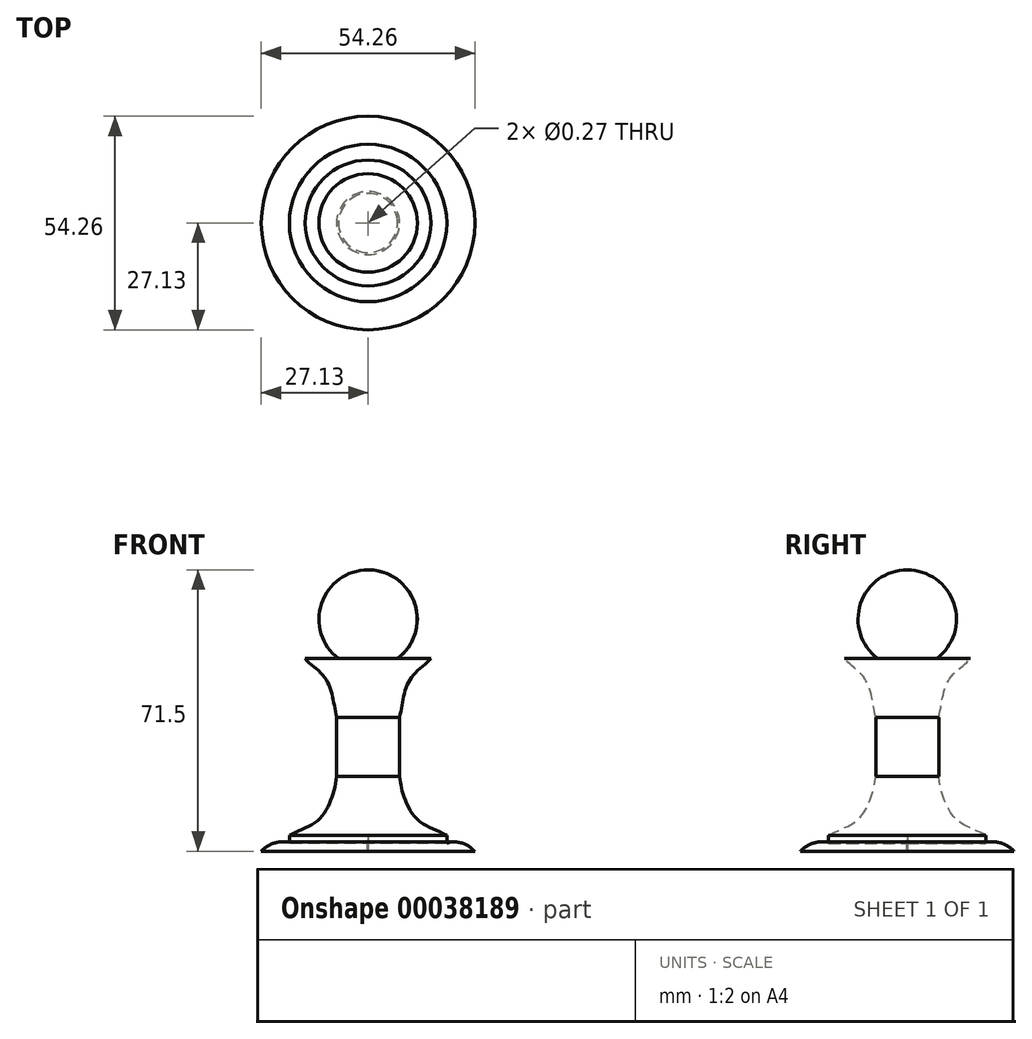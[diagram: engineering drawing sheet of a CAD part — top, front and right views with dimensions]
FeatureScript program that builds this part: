
annotation { "Feature Type Name" : "Feature", "Feature Type Description" : "" }
export const myFeature = defineFeature(function(context is Context, id is Id, definition is map)
    precondition{}
    {
        {
            var Q0;
            Q0=qCreatedBy(makeId("Front.planeOp"),FACE);
            var sketch = newSketch(context, id + "F0", { "sketchPlane" : qUnion([Q0])});
            skArc(sketch, "E0", {"start": v(7.5, -2.41) * mm, "mid": v(11.86, 11.54) * mm, "end": v(0, 20.09) * mm});
            skLineSegment(sketch, "E1", {"start": v(0, 7.59) * mm, "end": v(0, -2.41) * mm});
            skLineSegment(sketch, "E2", {"start": v(7.5, -2.41) * mm, "end": v(16, -2.41) * mm});
            skLineSegment(sketch, "E3", {"start": v(0, -2.41) * mm, "end": v(0, -17.41) * mm});
            skLineSegment(sketch, "E4", {"start": v(8, -17.41) * mm, "end": v(8, -32.41) * mm});
            skLineSegment(sketch, "E5", {"start": v(0, -32.41) * mm, "end": v(0, -47.41) * mm});
            skLineSegment(sketch, "E6", {"start": v(0, -47.41) * mm, "end": v(0.13, -49.4) * mm});
            skLineSegment(sketch, "E7", {"start": v(0.13, -49.4) * mm, "end": v(0.13, -51.4) * mm});
            skLineSegment(sketch, "E8", {"start": v(0, 20.09) * mm, "end": v(0, 7.59) * mm});
            skFitSpline(sketch, "E9", {"points": [v(16, -2.41) * mm, v(11.63, -6.46) * mm, v(9.18, -11.46) * mm, v(8, -17.41) * mm], "startDerivative": vector(-9.63, -12.6) * mm, "endDerivative": vector(-4.17, -18.05) * mm});
            skLineSegment(sketch, "E10", {"start": v(0.13, -51.4) * mm, "end": v(27.13, -51.4) * mm});
            skFitSpline(sketch, "E11", {"points": [v(8, -32.41) * mm, v(9.05, -37.26) * mm, v(12.81, -43.59) * mm, v(20, -47.41) * mm], "startDerivative": vector(1.61, -16.68) * mm, "endDerivative": vector(18.23, -11.03) * mm});
            skLineSegment(sketch, "E12", {"start": v(20, -47.41) * mm, "end": v(20, -49.4) * mm});
            skFitSpline(sketch, "E13", {"points": [v(20, -49.4) * mm, v(24.13, -49.4) * mm, v(27.13, -51.4) * mm], "startDerivative": vector(6.76, 3.7) * mm, "endDerivative": vector(6.97, -6.87) * mm});
            skLineSegment(sketch, "E14", {"start": v(0, -17.41) * mm, "end": v(0, -32.41) * mm});
            skSolve(sketch);
        }
        {
            var Q0;
            {var subQ2=sQuery(id+"F0.wireOp",EDGE,"E0");Q0=makeQuery(id+"F0.imprint","IMPRINT",FACE,{"disambiguationData":[TD([[makeQuery(id+"F0.imprint","IMPRINT",EDGE,{"derivedFrom":subQ2}),1.0]])]});}
            var Q1;
            {var subQ1=sQuery(id+"F0.wireOp",EDGE,"E3");Q1=makeQuery(id+"F0.imprint","IMPRINT",FACE,{"disambiguationData":[TD([[makeQuery(id+"F0.imprint","IMPRINT",EDGE,{"derivedFrom":subQ1}),1.0]])]});}
            var Q2;
            Q2=makeQuery(id+"F0.imprint","IMPRINT",FACE,{"disambiguationData":[TD([[makeQuery(id+"F0.imprint","IMPRINT",EDGE,{"derivedFrom":sQuery(id+"F0.wireOp",EDGE,"85af6ad6-df83-49e5-ba40-e06844bb0152")}),-1.0]])]});
            var Q3;
            Q3=makeQuery(id+"F0.imprint","IMPRINT",FACE,{"disambiguationData":[TD([[makeQuery(id+"F0.imprint","IMPRINT",EDGE,{"derivedFrom":sQuery(id+"F0.wireOp",EDGE,"0376ac24-ff57-42a7-9ef6-cdb5cd9e3d43")}),1.0]])]});
            var Q4;
            {var subQ2=sQuery(id+"F0.wireOp",EDGE,"E6");Q4=makeQuery(id+"F0.imprint","IMPRINT",FACE,{"disambiguationData":[TD([[makeQuery(id+"F0.imprint","IMPRINT",EDGE,{"derivedFrom":subQ2}),1.0]])]});}
            var Q5;
            {var subQ4=sQuery(id+"F0.wireOp",EDGE,"E7");Q5=makeQuery(id+"F0.imprint","IMPRINT",FACE,{"disambiguationData":[TD([[makeQuery(id+"F0.imprint","IMPRINT",EDGE,{"derivedFrom":subQ4}),1.0]])]});}
            var Q6;
            Q6=sQuery(id+"F0.wireOp",EDGE,"E8");
            revolve(context, id + "F1", {"entities" : qUnion([Q0, Q1, Q2, Q3, Q4, Q5]), "axis" : qUnion([Q6]), "revolveType" : RevolveType.FULL});
        }
    });
